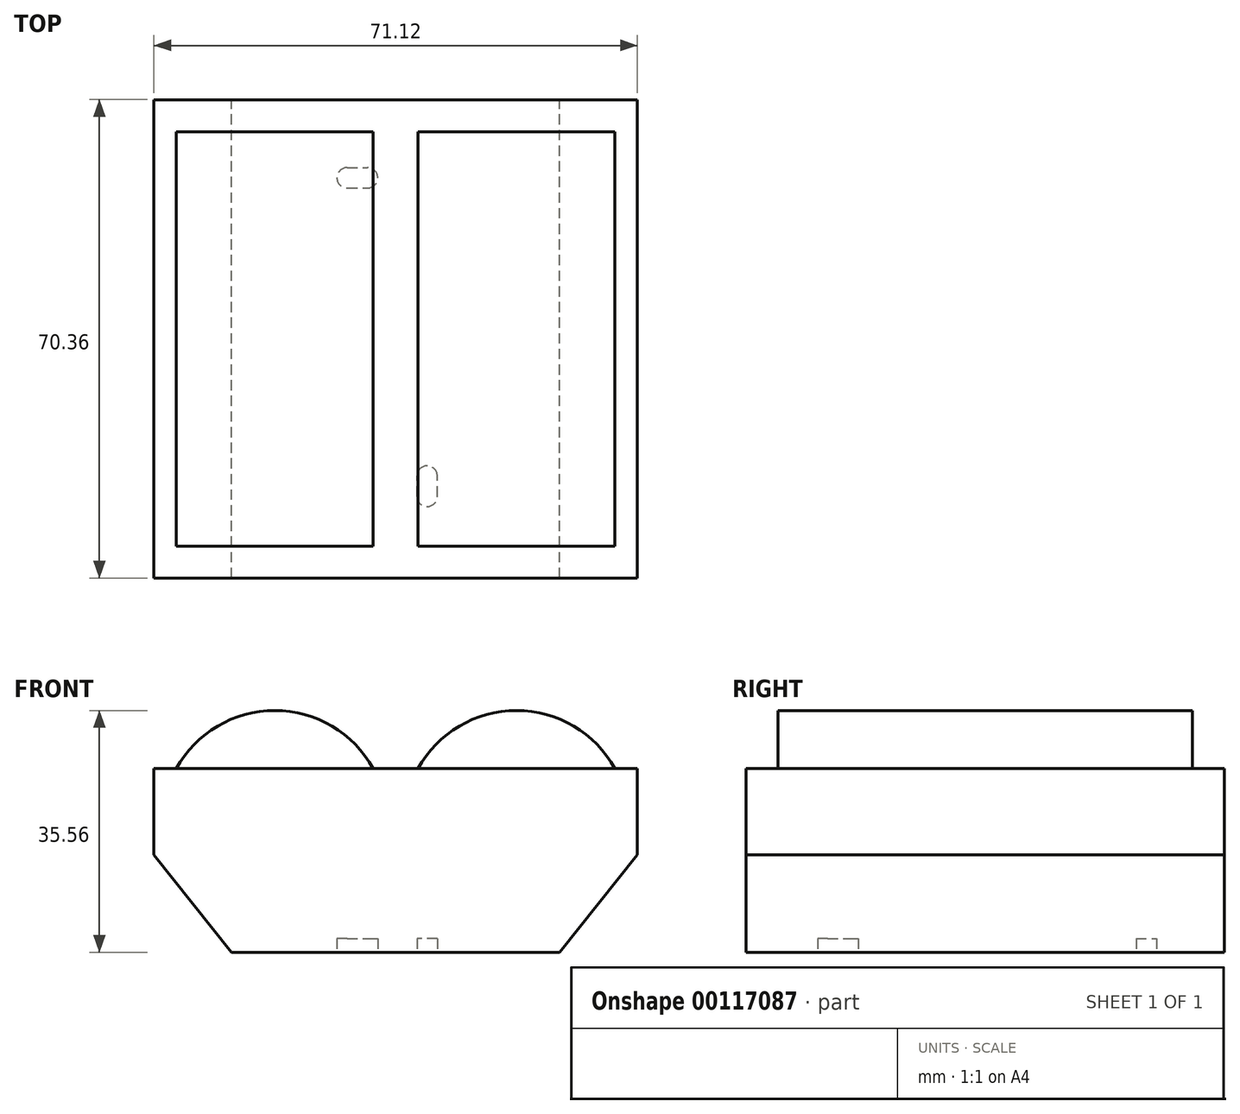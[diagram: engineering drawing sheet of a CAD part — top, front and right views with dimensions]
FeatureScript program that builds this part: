
annotation { "Feature Type Name" : "Feature", "Feature Type Description" : "" }
export const myFeature = defineFeature(function(context is Context, id is Id, definition is map)
    precondition{}
    {
        {
            var Q0;
            Q0=qCreatedBy(makeId("Front.planeOp"),FACE);
            var sketch = newSketch(context, id + "F0", { "sketchPlane" : qUnion([Q0])});
            skLineSegment(sketch, "E0", {"start": v(-24.13, 0) * mm, "end": v(24.13, 0) * mm});
            skLineSegment(sketch, "E1", {"start": v(24.13, 0) * mm, "end": v(35.56, 14.3) * mm});
            skLineSegment(sketch, "E2", {"start": v(35.56, 14.3) * mm, "end": v(35.56, 27) * mm});
            skLineSegment(sketch, "E3", {"start": v(35.56, 27) * mm, "end": v(-35.56, 27) * mm});
            skLineSegment(sketch, "E4", {"start": v(-35.56, 27) * mm, "end": v(-35.56, 14.3) * mm});
            skLineSegment(sketch, "E5", {"start": v(-35.56, 14.3) * mm, "end": v(-24.13, 0) * mm});
            skSolve(sketch);
        }
        {
            var Q0;
            Q0=qCreatedBy(makeId("Front.planeOp"),FACE);
            var sketch = newSketch(context, id + "F1", { "sketchPlane" : qUnion([Q0])});
            skPoint(sketch, "E6", {"position": v(0, 27) * mm});
            skPoint(sketch, "E7", {"position": v(17.78, 27) * mm});
            skCircle(sketch, "E8", {"center": v(17.78, 19.05) * mm, "radius": 16.51 * mm});
            skLineSegment(sketch, "E9", {"start": v(-38.5, 35.56) * mm, "end": v(41.98, 35.56) * mm, "construction": true});
            skCircle(sketch, "E10.MirrorC", {"center": v(-17.78, 19.05) * mm, "radius": 16.51 * mm});
            skSolve(sketch);
        }
        {
            var Q0;
            Q0 = qSketchRegion(id + "F0", true);
            extrude(context, id + "F2", {"entities" : qUnion([Q0]), "depth" : 70.36 * mm, "symmetric" : true});
        }
        {
            var Q0;
            Q0 = qSketchRegion(id + "F1", true);
            extrude(context, id + "F3", {"entities" : qUnion([Q0]), "operationType" : NewBodyOperationType.ADD, "depth" : 60.96 * mm, "symmetric" : true});
        }
        {
            var Q0;
            Q0=makeQuery(id+"F2.opExtrude","SWEPT_FACE",FACE,{"disambiguationData":[OSD([sQuery(id+"F0.wireOp",EDGE,"E0")])]});
            var sketch = newSketch(context, id + "F4", { "sketchPlane" : qUnion([Q0])});
            skLineSegment(sketch, "E11", {"start": v(4.63, 23.18) * mm, "end": v(4.63, 20.18) * mm});
            skArc(sketch, "E12.0.startCap", {"start": v(3.13, 23.18) * mm, "mid": v(4.63, 24.68) * mm, "end": v(6.13, 23.18) * mm});
            skArc(sketch, "E12.0.endCap", {"start": v(6.13, 20.18) * mm, "mid": v(4.63, 18.68) * mm, "end": v(3.13, 20.18) * mm});
            skLineSegment(sketch, "E12.0.left", {"start": v(6.13, 23.18) * mm, "end": v(6.13, 20.18) * mm});
            skLineSegment(sketch, "E12.0.right", {"start": v(3.13, 23.18) * mm, "end": v(3.13, 20.18) * mm});
            skLineSegment(sketch, "E13", {"start": v(-7.13, -23.68) * mm, "end": v(-4.13, -23.68) * mm});
            skArc(sketch, "E14.0.startCap", {"start": v(-7.13, -25.18) * mm, "mid": v(-8.63, -23.68) * mm, "end": v(-7.13, -22.18) * mm});
            skArc(sketch, "E14.0.endCap", {"start": v(-4.13, -22.18) * mm, "mid": v(-2.63, -23.68) * mm, "end": v(-4.13, -25.18) * mm});
            skLineSegment(sketch, "E14.0.left", {"start": v(-7.13, -22.18) * mm, "end": v(-4.13, -22.18) * mm});
            skLineSegment(sketch, "E14.0.right", {"start": v(-7.13, -25.18) * mm, "end": v(-4.13, -25.18) * mm});
            skSolve(sketch);
        }
        {
            var Q0;
            Q0 = qSketchRegion(id + "F4", true);
            extrude(context, id + "F5", {"entities" : qUnion([Q0]), "operationType" : NewBodyOperationType.REMOVE, "oppositeDirection" : true, "depth" : 2 * mm});
        }
    });
